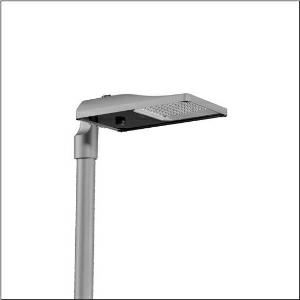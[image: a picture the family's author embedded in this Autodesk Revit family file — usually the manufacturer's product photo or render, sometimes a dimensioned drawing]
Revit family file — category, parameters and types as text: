
# Revit family: streetlight_sl_31_midi___st0_5a_5xh7b31t08na_48dc
name_source: partatom
category: Lighting Fixtures
units: mm (PartAtom-declared; Revit-internal decimal feet)

## family parameters
Cut with Voids When Loaded = No
Host = Face
Light Source = No
Part Type = Normal
Room Calculation Point = No
Round Connector Dimension = Use Diameter
Shared = No

## types (1)
- --- (1 x LED, 22750 lm, 149.5 W, 3000K)
    Apparent Load = 149 VA
    CIE Flux Codes = 43 76 97 100 100
    Color Rendering = 70
    Color Temperature = 3000K
    Default Elevation = 1800 mm
    Description = Streetlight SL 31 midi D4i, Desk-Remote mast luminaire for post-top, side-entry; light control with lens of PMMA; light distribution: ST0.5a, direct asymmetric distribution, for standard-compliant lighting for roads and squares; LED: luminous flux: 22.750lm, light colour: 730, colour temperature: 3000K; luminous efficacy: 152,2lm/W; control: pre-setting: logarithmic dimming characteristic, flexible luminous flux parameterisation, time-dependent luminous flux control, constant luminous flux control, power reduction, intelligent temperature release in ECG and LED module, overheat protection; luminaire housing, of diecast aluminium, SITECO metallic grey (DB 702S), corrosivity category C5 high according to DIN EN ISO 12944; cover of toughened safety glass, transparent, opened without tools; mast flange of diecast aluminium, SITECO metallic grey (DB 702S), spigot size: 76/60mm, mast flange included unmounted; cable length: 12,5m, connection cable pre-assembled; mains connection: 220..240V, AC, 50/60Hz; power consumption (at start of service life): 149,5W / (at end of service life): 163,6W / (with reduced operation 50%): 66,6W; protection rating (complete): IP66; insulation class (complete): insulation class II (safety insulation); impact resistance: IK09; certification: CE, ENEC, ENEC+, VDE, UKCA, ZD4i; permissible operating ambient temperature for outdoor applications: -40..+50°C; packaging unit: 1 piece

Light Distribution: ST0.5a
    Height = 79 mm
    Lamp = 1 x LED
    Lamp Light Flux = 22750 lm
    Lamp Power = 149.5 W
    Lamp count = 1
    Length = 577 mm
    Luminous efficacy = 152 lm/W
    Manufacturer = Siteco
    ModVariant = No
    Model = 5XH7B31T08NA
    Number of Poles = 1
    OnlyDefault = Yes
    Power Factor = 1
    Product Name = Streetlight SL 31 midi | ST0.5a
    Product group = mast luminaire | pylon top
    ProductGroupID = 6100
    Protection Class = Protection class II
    Protection Degree = IP 66
    RLX_Detail_Level = 1
    RLX_Emergency_Light_Flux = 0 lm
    RLX_Emergency_Type = 0
    RLX_Emergency_Type_DB = No
    RlxData = <blob elided: 54161 chars, md5=52dd9019>
    Socket = socket
    Standby Power = 0 W
    System Light Flux = 22749 lm
    System Power = 149 W
    Type Comments = factory setting: luminous flux: 100 % | dim-lin: 254 | 795 mA
    Type Image = l_1300321.jpg
    URL = http://relux.com
    VarID = @adj_064117
    Voltage = 0 V
    Weight = 0.00 kg
    Width = 362 mm

## geometry (parser evidence)
native form markers: Blend x4, Sweep x10
no freeform markers — native parametric forms only
